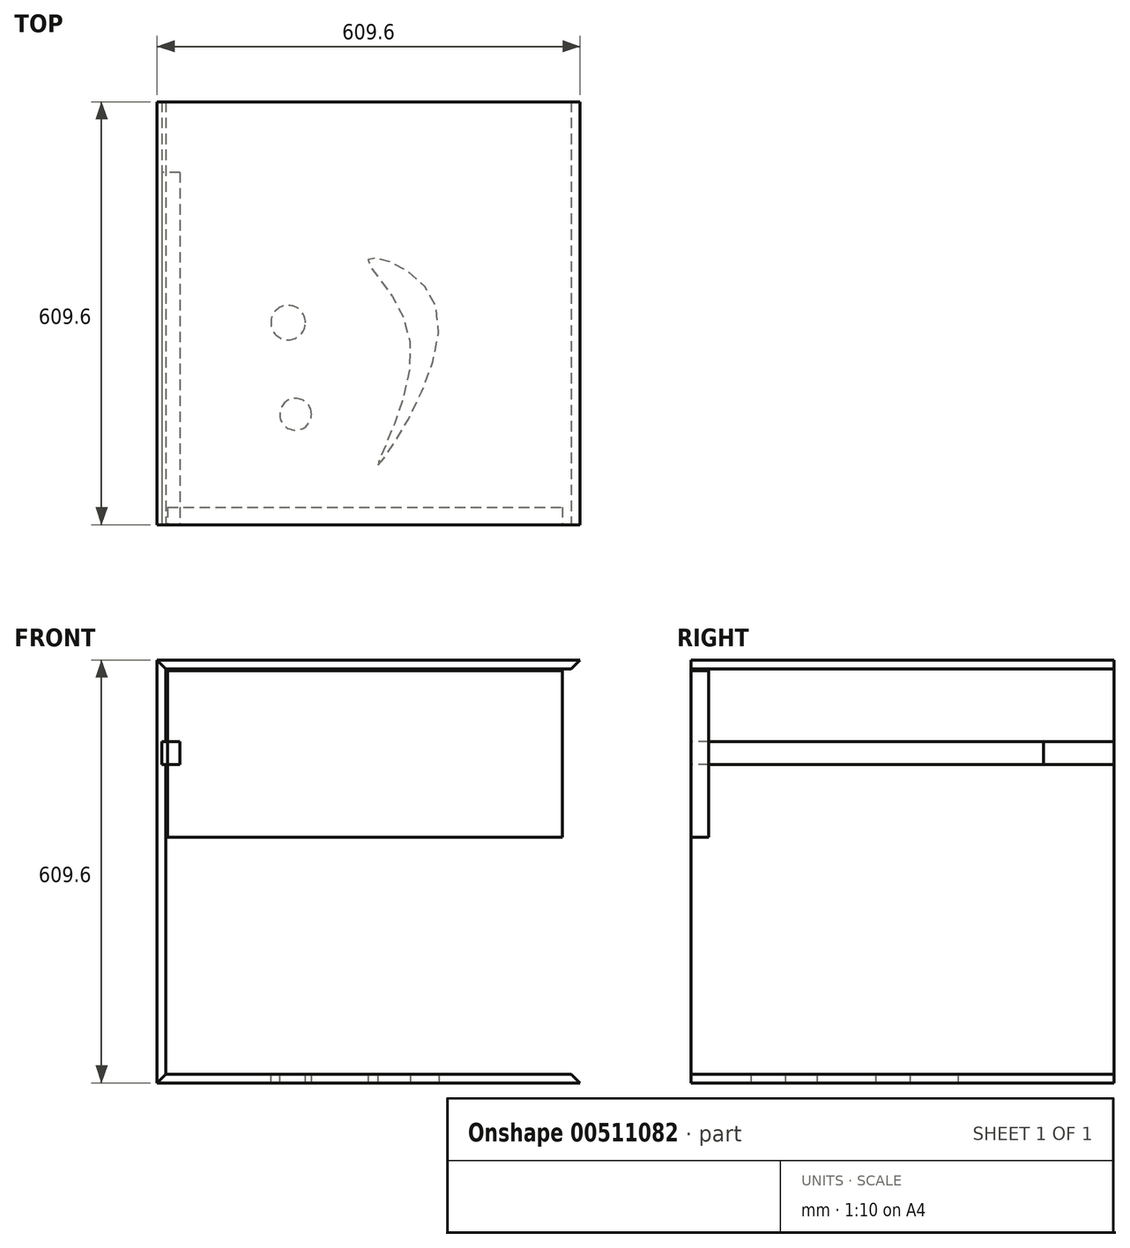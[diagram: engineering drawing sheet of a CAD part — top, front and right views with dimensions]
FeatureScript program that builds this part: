
annotation { "Feature Type Name" : "Feature", "Feature Type Description" : "" }
export const myFeature = defineFeature(function(context is Context, id is Id, definition is map)
    precondition{}
    {
        {
            var Q0;
            Q0=qCreatedBy(makeId("Front.planeOp"),FACE);
            var sketch = newSketch(context, id + "F0", { "sketchPlane" : qUnion([Q0])});
            skLineSegment(sketch, "E0.bottom", {"start": v(304.8, 304.8) * mm, "end": v(-304.8, 304.8) * mm});
            skLineSegment(sketch, "E0.top", {"start": v(304.8, -304.8) * mm, "end": v(-304.8, -304.8) * mm});
            skLineSegment(sketch, "E0.left", {"start": v(304.8, 304.8) * mm, "end": v(304.8, -304.8) * mm});
            skLineSegment(sketch, "E0.right", {"start": v(-304.8, 304.8) * mm, "end": v(-304.8, -304.8) * mm});
            skPoint(sketch, "E0.middle", {"position": v(0, 0) * mm});
            skLineSegment(sketch, "E1.bottom", {"start": v(292.1, 292.1) * mm, "end": v(-292.1, 292.1) * mm});
            skLineSegment(sketch, "E1.top", {"start": v(292.1, -292.1) * mm, "end": v(-292.1, -292.1) * mm});
            skLineSegment(sketch, "E1.left", {"start": v(292.1, 292.1) * mm, "end": v(292.1, -292.1) * mm});
            skLineSegment(sketch, "E1.right", {"start": v(-292.1, 292.1) * mm, "end": v(-292.1, -292.1) * mm});
            skLineSegment(sketch, "E2", {"start": v(-304.8, 304.8) * mm, "end": v(-292.1, 292.1) * mm});
            skLineSegment(sketch, "E3", {"start": v(292.1, 292.1) * mm, "end": v(304.8, 304.8) * mm});
            skLineSegment(sketch, "E4", {"start": v(292.1, -292.1) * mm, "end": v(304.8, -304.8) * mm});
            skLineSegment(sketch, "E5", {"start": v(-292.1, -292.1) * mm, "end": v(-304.8, -304.8) * mm});
            skLineSegment(sketch, "E6.bottom", {"start": v(-289.56, 289.56) * mm, "end": v(279.13, 289.56) * mm});
            skLineSegment(sketch, "E6.top", {"start": v(-289.56, 49.39) * mm, "end": v(279.13, 49.39) * mm});
            skLineSegment(sketch, "E6.left", {"start": v(-289.56, 289.56) * mm, "end": v(-289.56, 49.39) * mm});
            skLineSegment(sketch, "E6.right", {"start": v(279.13, 289.56) * mm, "end": v(279.13, 49.39) * mm});
            skLineSegment(sketch, "E7.bottom", {"start": v(-271.68, 187.07) * mm, "end": v(-297.81, 187.07) * mm});
            skLineSegment(sketch, "E7.top", {"start": v(-271.68, 154.25) * mm, "end": v(-297.81, 154.25) * mm});
            skLineSegment(sketch, "E7.left", {"start": v(-271.68, 187.07) * mm, "end": v(-271.68, 154.25) * mm});
            skLineSegment(sketch, "E7.right", {"start": v(-297.81, 187.07) * mm, "end": v(-297.81, 154.25) * mm});
            skSolve(sketch);
        }
        {
            var Q0;
            Q0=makeQuery(id+"F0.imprint","IMPRINT",FACE,{"disambiguationData":[TD([[makeQuery(id+"F0.imprint","IMPRINT",EDGE,{"derivedFrom":sQuery(id+"F0.wireOp",EDGE,"E0.bottom")}),1.0]])]});
            extrude(context, id + "F1", {"entities" : qUnion([Q0]), "oppositeDirection" : true, "depth" : 609.6 * mm, "offsetDistance" : 25.4 * mm});
        }
        {
            var Q0;
            Q0=makeQuery(id+"F0.imprint","IMPRINT",FACE,{"disambiguationData":[TD([[makeQuery(id+"F0.imprint","IMPRINT",EDGE,{"derivedFrom":sQuery(id+"F0.wireOp",EDGE,"E0.right")}),1.0]])]});
            var Q1;
            Q1=makeQuery(id+"F1.opExtrude","CAP_VERTEX",VERTEX,{"disambiguationData":[OSD([sQuery(id+"F0.wireOp",EDGE,"E0.bottom"),sQuery(id+"F0.wireOp",EDGE,"E0.right"),sQuery(id+"F0.wireOp",EDGE,"E2")])],"isStart":false});
            extrude(context, id + "F2", {"entities" : qUnion([Q0]), "endBound" : BoundingType.UP_TO_VERTEX, "oppositeDirection" : true, "depth" : 25.4 * mm, "endBoundEntityVertex" : qUnion([Q1]), "offsetDistance" : 25.4 * mm});
        }
        {
            var Q0;
            Q0=makeQuery(id+"F0.imprint","IMPRINT",FACE,{"disambiguationData":[TD([[makeQuery(id+"F0.imprint","IMPRINT",EDGE,{"derivedFrom":sQuery(id+"F0.wireOp",EDGE,"E0.top")}),-1.0]])]});
            var Q1;
            Q1=makeQuery(id+"F1.opExtrude","CAP_VERTEX",VERTEX,{"disambiguationData":[OSD([sQuery(id+"F0.wireOp",EDGE,"E0.bottom"),sQuery(id+"F0.wireOp",EDGE,"E0.right"),sQuery(id+"F0.wireOp",EDGE,"E2")])],"isStart":false});
            extrude(context, id + "F3", {"entities" : qUnion([Q0]), "endBound" : BoundingType.UP_TO_VERTEX, "oppositeDirection" : true, "depth" : 25.4 * mm, "endBoundEntityVertex" : qUnion([Q1]), "offsetDistance" : 25.4 * mm});
        }
        {
            var Q0;
            {var subQ4=sQuery(id+"F0.wireOp",EDGE,"E6.bottom");Q0=makeQuery(id+"F0.imprint","IMPRINT",FACE,{"disambiguationData":[TD([[makeQuery(id+"F0.imprint","IMPRINT",EDGE,{"derivedFrom":subQ4}),-1.0]])]});}
            var Q1;
            {var subQ5=sQuery(id+"F0.wireOp",EDGE,"E7.left");Q1=makeQuery(id+"F0.imprint","IMPRINT",FACE,{"disambiguationData":[TD([[makeQuery(id+"F0.imprint","IMPRINT",EDGE,{"derivedFrom":subQ5}),-1.0]])]});}
            extrude(context, id + "F4", {"entities" : qUnion([Q0, Q1]), "oppositeDirection" : true, "depth" : 25.4 * mm, "offsetDistance" : 25.4 * mm});
        }
        {
            var Q0;
            {var subQ5=sQuery(id+"F0.wireOp",EDGE,"E7.left");Q0=makeQuery(id+"F0.imprint","IMPRINT",FACE,{"disambiguationData":[TD([[makeQuery(id+"F0.imprint","IMPRINT",EDGE,{"derivedFrom":subQ5}),-1.0]])]});}
            var Q1;
            {var subQ5=sQuery(id+"F0.wireOp",EDGE,"E7.right");Q1=makeQuery(id+"F0.imprint","IMPRINT",FACE,{"disambiguationData":[TD([[makeQuery(id+"F0.imprint","IMPRINT",EDGE,{"derivedFrom":subQ5}),1.0]])]});}
            var Q2;
            {var subQ0=sQuery(id+"F0.wireOp",EDGE,"E7.bottom");var subQ1=sQuery(id+"F0.wireOp",EDGE,"E1.right");var subQ2=makeQuery(id+"F0.imprint","INTERSECT",VERTEX,{"derivedFrom":[subQ1,subQ0]});Q2=makeQuery(id+"F0.imprint","IMPRINT",FACE,{"disambiguationData":[TD([[makeQuery(id+"F0.imprint","IMPRINT",EDGE,{"disambiguationData":[TD([[subQ2,-1.0]])],"derivedFrom":subQ1}),1.0]])]});}
            var Q3;
            Q3=sQuery(id+"F0.wireOp",EDGE,"E7.bottom");
            extrude(context, id + "F5", {"entities" : qUnion([Q0, Q1, Q2]), "surfaceEntities" : qUnion([Q3]), "oppositeDirection" : true, "depth" : 508 * mm, "offsetDistance" : 25.4 * mm});
        }
        {
            var Q0;
            Q0=qCreatedBy(makeId("Top.planeOp"),FACE);
            var sketch = newSketch(context, id + "F6", { "sketchPlane" : qUnion([Q0])});
            skCircle(sketch, "E8", {"center": v(-105.17, 159.1) * mm, "radius": 22.88 * mm});
            skCircle(sketch, "E9", {"center": v(-115.95, 291.23) * mm, "radius": 24.86 * mm});
            skFitSpline(sketch, "E10", {"points": [v(13.48, 86.29) * mm, v(98.42, 310.1) * mm, v(0, 382.9) * mm, v(59.32, 265.6) * mm, v(13.48, 86.29) * mm]});
            skSolve(sketch);
        }
        {
            var Q0;
            Q0 = qSketchRegion(id + "F6", true);
            extrude(context, id + "F7", {"entities" : qUnion([Q0]), "operationType" : NewBodyOperationType.REMOVE, "endBound" : BoundingType.THROUGH_ALL, "oppositeDirection" : true, "depth" : 25.4 * mm, "offsetDistance" : 25.4 * mm});
        }
    });
